# Revit family: QF_ZANUSSI_110551_ZBFA22RPE
name_source: partatom
category: Specialty Equipment
revit_build: Autodesk Revit 2018 (Build: 20190510_1515(x64)
units: mm (PartAtom-declared; Revit-internal decimal feet)

## family parameters
Always vertical = Yes
Cut with Voids When Loaded = No
Part Type = Normal
Room Calculation Point = No
Round Connector Dimension = Use Radius
Shared = Yes
Work Plane-Based = No

## types (1)
- QF_ZANUSSI_110551_ZBFA22RPE
    Accessory = Yes
    Cold Water Size = 0"
    Compressed Air Pressure = 0.00 psi
    Compressed Air Size = 0"
    Compressed Air Volume = 0 GPM
    Condensate Return Size = 0"
    Cycle = 60 Hz
    Depth Actual = 1395 mm
    Description = RAPIDO BLAST CHILLER FREEZER 200/170KG 20 GN 2/1 - PASS-THROUGH - REMOTE REFRIGERATING UNIT
    Gas Input Pressure = 0.0
    Gas KW = 0
    Gas Size = 0"
    HP = 3 HP
    Height Actual = 2270 mm  [stored 7.44751 ft]
    Hot Water Size = 0"
    Item Number = 110551
    Length Actual = 1400 mm  [stored 4.59318 ft]
    Manufacturer = Zanussi
    Model = ZBFA22RPE
    Phase = 3
    Refrigerant Compressor Remote = Yes
    Refrigeration Liquid Line Size = 0"
    Refrigeration Suction Line Size = 0"
    Steam Pounds per Hour = 0
    Steam Supply Maximum Pressure = 0.00 psi
    Steam Supply Minimum Pressure = 0.00 psi
    Steam Supply Size = 0"
    URL = http://www.zanussiprofessional.com
    URL Manufacturer = http://www.zanussiprofessional.com
    Volts = 380 V
    Watts = 209 W
    Weight = 0.00 kg

note: source unit labels omitted for Gas Input Pressure — the stored unit's dimension contradicts the parameter name (converter mislabeling)

note: [stored X ft] marks values corroborated as IEEE doubles in the binary element streams (Revit-internal decimal feet)

## geometry (parser evidence)
native form markers: Sweep x3
no freeform markers — native parametric forms only
